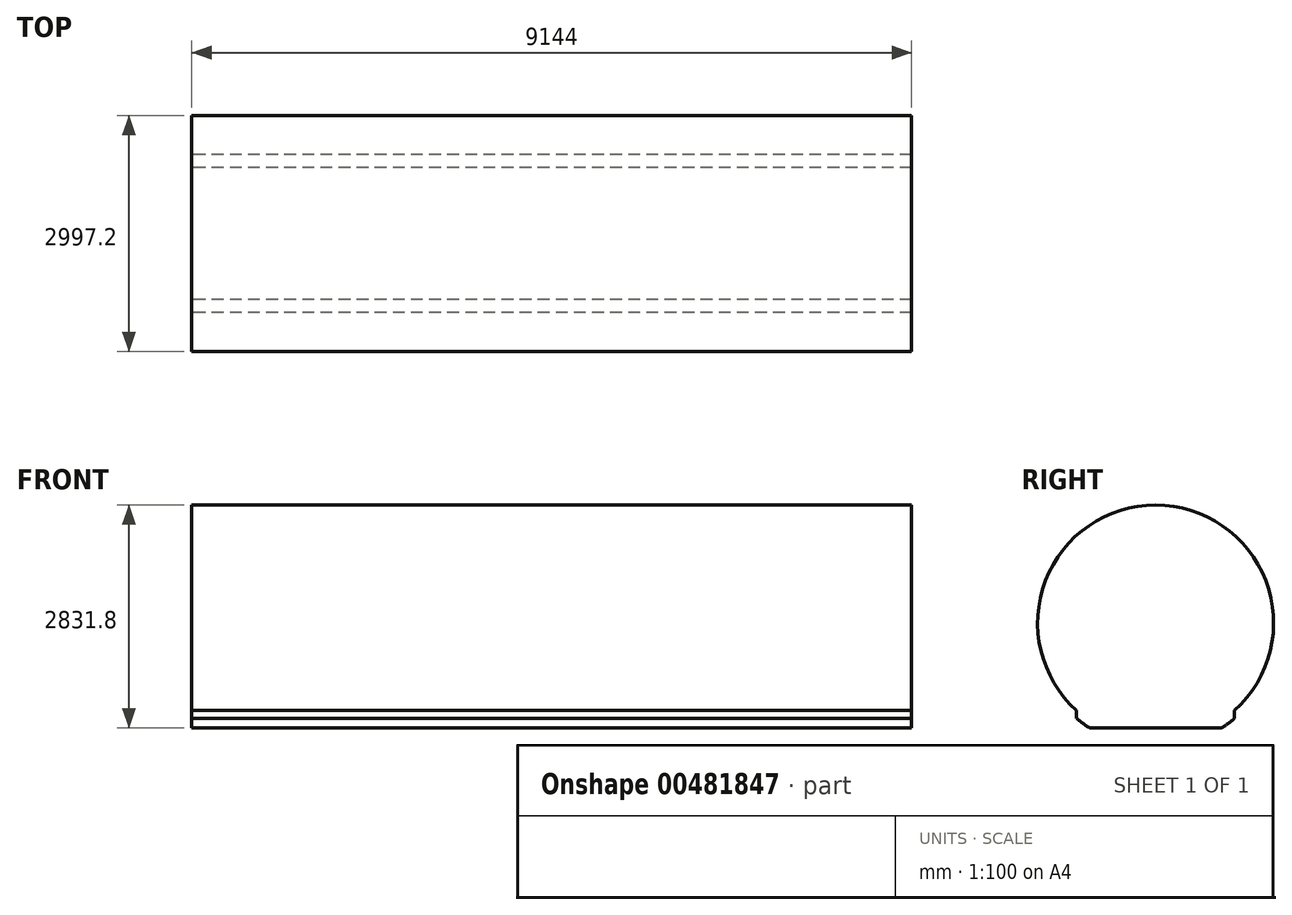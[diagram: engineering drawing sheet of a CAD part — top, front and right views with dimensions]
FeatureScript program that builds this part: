
annotation { "Feature Type Name" : "Feature", "Feature Type Description" : "" }
export const myFeature = defineFeature(function(context is Context, id is Id, definition is map)
    precondition{}
    {
        {
            var Q0;
            Q0=qCreatedBy(makeId("Right.planeOp"),FACE);
            var sketch = newSketch(context, id + "F0", { "sketchPlane" : qUnion([Q0])});
            skArc(sketch, "E0", {"start": v(-1003.3, -1213.83) * mm, "mid": v(-922.68, -1276.19) * mm, "end": v(-838.2, -1333.2) * mm});
            skArc(sketch, "E1", {"start": v(1003.3, -1113.19) * mm, "mid": v(0, 1498.6) * mm, "end": v(-1003.3, -1113.19) * mm});
            skLineSegment(sketch, "E2", {"start": v(-838.2, -1333.2) * mm, "end": v(838.2, -1333.2) * mm});
            skLineSegment(sketch, "E3", {"start": v(-1003.3, -1113.19) * mm, "end": v(-1003.3, -1213.83) * mm});
            skLineSegment(sketch, "E4", {"start": v(1003.3, -1113.19) * mm, "end": v(1003.3, -1213.83) * mm});
            skArc(sketch, "E5.trimOffspring", {"start": v(838.2, -1333.2) * mm, "mid": v(922.68, -1276.19) * mm, "end": v(1003.3, -1213.83) * mm});
            skLineSegment(sketch, "E6", {"start": v(0, -1333.2) * mm, "end": v(0, 1498.6) * mm});
            skSolve(sketch);
        }
        {
            var Q0;
            Q0 = qSketchRegion(id + "F0", true);
            extrude(context, id + "F1", {"entities" : qUnion([Q0]), "depth" : 9144 * mm});
        }
    });
